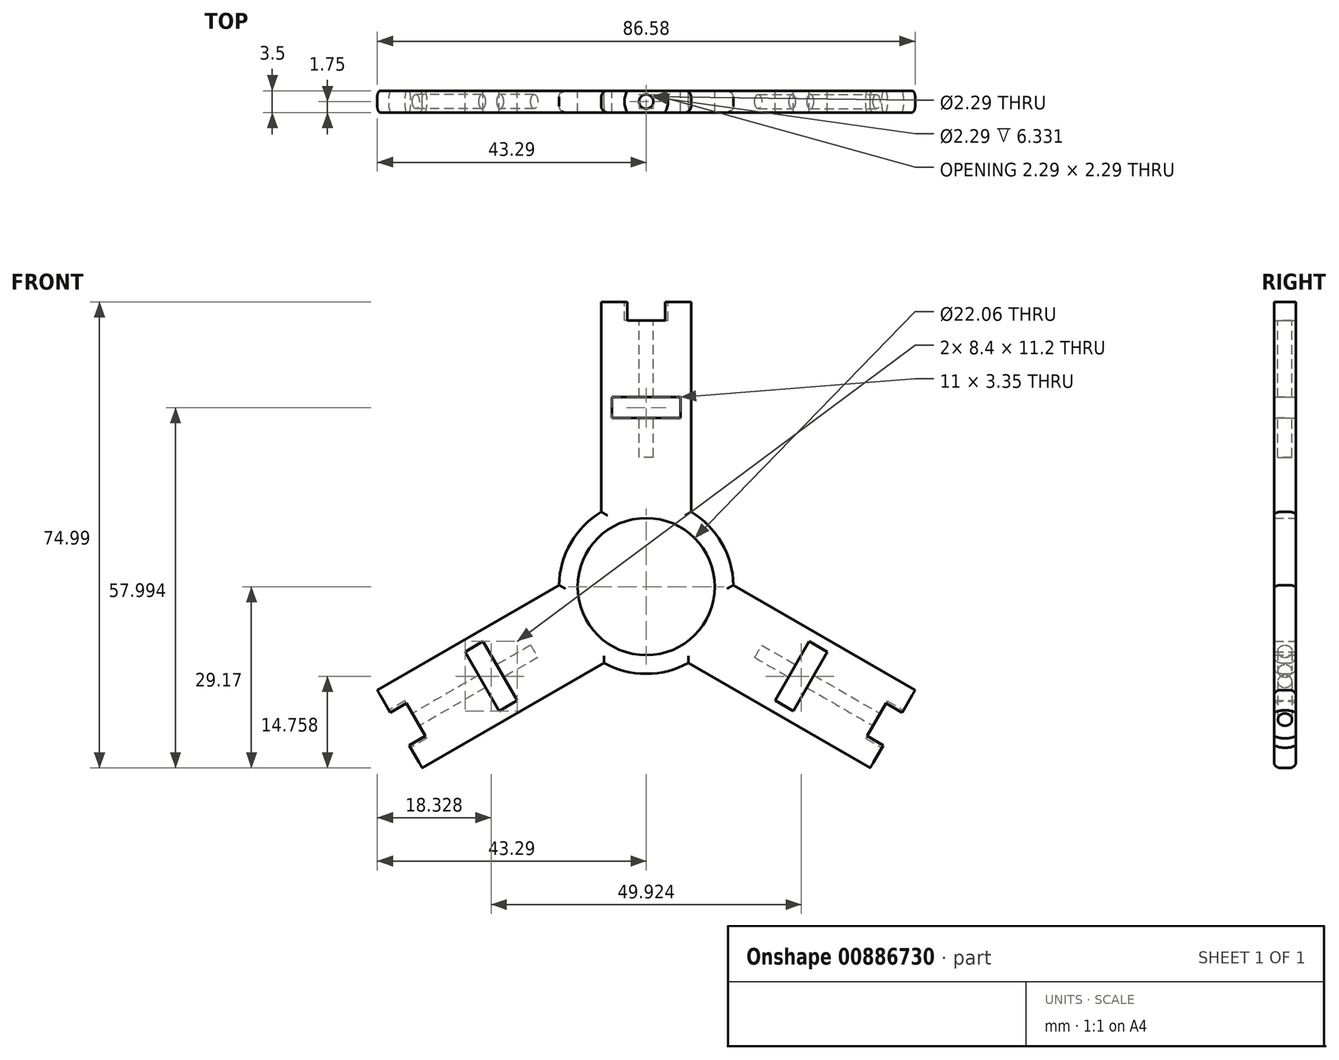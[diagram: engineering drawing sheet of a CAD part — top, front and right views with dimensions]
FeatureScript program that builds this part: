
annotation { "Feature Type Name" : "Feature", "Feature Type Description" : "" }
export const myFeature = defineFeature(function(context is Context, id is Id, definition is map)
    precondition{}
    {
        {
            var Q0;
            Q0=qCreatedBy(makeId("Front.planeOp"),FACE);
            var sketch = newSketch(context, id + "F0", { "sketchPlane" : qUnion([Q0])});
            skCircle(sketch, "E0", {"center": v(0, 0) * mm, "radius": 11.03 * mm});
            skCircle(sketch, "E1.0", {"center": v(0, 0) * mm, "radius": 14.03 * mm});
            skSolve(sketch);
        }
        {
            var Q0;
            Q0=qCreatedBy(makeId("Front.planeOp"),FACE);
            var sketch = newSketch(context, id + "F1", { "sketchPlane" : qUnion([Q0])});
            skLineSegment(sketch, "E2.bottom", {"start": v(0, 0) * mm, "end": v(-7.23, 0) * mm});
            skLineSegment(sketch, "E2.top", {"start": v(0, 45.82) * mm, "end": v(-7.23, 45.82) * mm});
            skLineSegment(sketch, "E2.left", {"start": v(0, 0) * mm, "end": v(0, 45.82) * mm});
            skLineSegment(sketch, "E2.right", {"start": v(-7.23, 0) * mm, "end": v(-7.23, 45.82) * mm});
            skLineSegment(sketch, "E3.MirrorCS", {"start": v(0, 0) * mm, "end": v(7.23, 0) * mm});
            skLineSegment(sketch, "E4.MirrorCS", {"start": v(0, 45.82) * mm, "end": v(7.23, 45.82) * mm});
            skLineSegment(sketch, "E5.MirrorCS", {"start": v(7.23, 0) * mm, "end": v(7.23, 45.82) * mm});
            skSolve(sketch);
        }
        {
            var Q0;
            Q0=makeQuery(id+"F0.imprint","IMPRINT",FACE,{"disambiguationData":[TD([[makeQuery(id+"F0.imprint","IMPRINT",EDGE,{"derivedFrom":sQuery(id+"F0.wireOp",EDGE,"E0")}),-1.0]])]});
            extrude(context, id + "F2", {"entities" : qUnion([Q0]), "endBound" : BoundingType.SYMMETRIC, "depth" : 3.5 * mm, "offsetDistance" : 25 * mm});
        }
        {
            var Q0;
            Q0=makeQuery(id+"F1.imprint","IMPRINT",FACE,{"disambiguationData":[TD([[makeQuery(id+"F1.imprint","IMPRINT",EDGE,{"derivedFrom":sQuery(id+"F1.wireOp",EDGE,"E2.left")}),-1.0]])]});
            var Q1;
            Q1=makeQuery(id+"F1.imprint","IMPRINT",FACE,{"disambiguationData":[TD([[makeQuery(id+"F1.imprint","IMPRINT",EDGE,{"derivedFrom":sQuery(id+"F1.wireOp",EDGE,"E2.bottom")}),-1.0]])]});
            extrude(context, id + "F3", {"entities" : qUnion([Q0, Q1]), "operationType" : NewBodyOperationType.ADD, "endBound" : BoundingType.SYMMETRIC, "depth" : 3.5 * mm, "offsetDistance" : 25 * mm});
        }
        {
            var Q0;
            Q0=makeQuery(id+"F3.opExtrude","SWEPT_FACE",FACE,{"disambiguationData":[OSD([sQuery(id+"F1.wireOp",EDGE,"E2.top"),sQuery(id+"F1.wireOp",EDGE,"E4.MirrorCS")])]});
            var sketch = newSketch(context, id + "F4", { "sketchPlane" : qUnion([Q0])});
            skCircle(sketch, "E6", {"center": v(0, 0) * mm, "radius": 3.5 * mm});
            skCircle(sketch, "E7", {"center": v(0, 0) * mm, "radius": 1.14 * mm});
            skSolve(sketch);
        }
        {
            var Q0;
            {var subQ0=sQuery(id+"F4.wireOp",EDGE,"E6");var subQ1=makeQuery(id+"F3.opExtrude","CAP_EDGE",EDGE,{"disambiguationData":[OSD([sQuery(id+"F1.wireOp",EDGE,"E2.top"),sQuery(id+"F1.wireOp",EDGE,"E4.MirrorCS")])],"isStart":false});var subQ2=makeQuery(id+"F4.imprint","INTERSECT",VERTEX,{"disambiguationData":[OD(0.0)],"derivedFrom":[subQ1,subQ0]});Q0=makeQuery(id+"F4.imprint","IMPRINT",FACE,{"disambiguationData":[TD([[makeQuery(id+"F4.imprint","IMPRINT",EDGE,{"disambiguationData":[TD([[subQ2,-1.0]])],"derivedFrom":subQ0}),1.0]])]});}
            var Q1;
            Q1=makeQuery(id+"F4.imprint","IMPRINT",FACE,{"disambiguationData":[TD([[makeQuery(id+"F4.imprint","IMPRINT",EDGE,{"derivedFrom":sQuery(id+"F4.wireOp",EDGE,"E7")}),-1.0]])]});
            var Q2;
            {var subQ0=sQuery(id+"F4.wireOp",EDGE,"E6");var subQ1=makeQuery(id+"F3.opExtrude","CAP_EDGE",EDGE,{"disambiguationData":[OSD([sQuery(id+"F1.wireOp",EDGE,"E2.top"),sQuery(id+"F1.wireOp",EDGE,"E4.MirrorCS")])],"isStart":true});var subQ2=makeQuery(id+"F4.imprint","INTERSECT",VERTEX,{"disambiguationData":[OD(0.0)],"derivedFrom":[subQ1,subQ0]});Q2=makeQuery(id+"F4.imprint","IMPRINT",FACE,{"disambiguationData":[TD([[makeQuery(id+"F4.imprint","IMPRINT",EDGE,{"disambiguationData":[TD([[subQ2,1.0]])],"derivedFrom":subQ0}),1.0]])]});}
            var Q3;
            Q3=makeQuery(id+"F4.imprint","IMPRINT",FACE,{"disambiguationData":[TD([[makeQuery(id+"F4.imprint","IMPRINT",EDGE,{"derivedFrom":sQuery(id+"F4.wireOp",EDGE,"E7")}),1.0]])]});
            extrude(context, id + "F5", {"entities" : qUnion([Q0, Q1, Q2, Q3]), "operationType" : NewBodyOperationType.REMOVE, "oppositeDirection" : true, "depth" : 3 * mm, "offsetDistance" : 25 * mm});
        }
        {
            var Q0;
            Q0=makeQuery(id+"F4.imprint","IMPRINT",FACE,{"disambiguationData":[TD([[makeQuery(id+"F4.imprint","IMPRINT",EDGE,{"derivedFrom":sQuery(id+"F4.wireOp",EDGE,"E7")}),1.0]])]});
            extrude(context, id + "F6", {"entities" : qUnion([Q0]), "operationType" : NewBodyOperationType.REMOVE, "oppositeDirection" : true, "depth" : 25 * mm, "offsetDistance" : 25 * mm});
        }
        {
            var Q0;
            Q0=makeQuery(id+"F3.boolean.opBoolean","MERGE",FACE,{"derivedFrom":[makeQuery(id+"F2.opExtrude","CAP_FACE",FACE,{"disambiguationData":[OSD([sQuery(id+"F0.wireOp",EDGE,"E0")])],"isStart":true}),makeQuery(id+"F3.opExtrude","CAP_FACE",FACE,{"disambiguationData":[OSD([sQuery(id+"F1.wireOp",EDGE,"E2.bottom"),sQuery(id+"F1.wireOp",EDGE,"E2.top"),sQuery(id+"F1.wireOp",EDGE,"E2.right"),sQuery(id+"F1.wireOp",EDGE,"E3.MirrorCS"),sQuery(id+"F1.wireOp",EDGE,"E4.MirrorCS"),sQuery(id+"F1.wireOp",EDGE,"E5.MirrorCS")])],"isStart":true})]});
            var sketch = newSketch(context, id + "F7", { "sketchPlane" : qUnion([Q0])});
            skLineSegment(sketch, "E8.bottom", {"start": v(0, 27.15) * mm, "end": v(5.5, 27.15) * mm});
            skLineSegment(sketch, "E8.top", {"start": v(0, 30.5) * mm, "end": v(5.5, 30.5) * mm});
            skLineSegment(sketch, "E8.left", {"start": v(0, 27.15) * mm, "end": v(0, 30.5) * mm});
            skLineSegment(sketch, "E8.right", {"start": v(5.5, 27.15) * mm, "end": v(5.5, 30.5) * mm});
            skLineSegment(sketch, "E9.MirrorCS", {"start": v(0, 30.5) * mm, "end": v(-5.5, 30.5) * mm});
            skLineSegment(sketch, "E10.MirrorCS", {"start": v(-5.5, 27.15) * mm, "end": v(-5.5, 30.5) * mm});
            skLineSegment(sketch, "E11.MirrorCS", {"start": v(0, 27.15) * mm, "end": v(-5.5, 27.15) * mm});
            skSolve(sketch);
        }
        {
            var Q0;
            Q0=qCreatedBy(makeId("Top.planeOp"),FACE);
            var sketch = newSketch(context, id + "F8", { "sketchPlane" : qUnion([Q0])});
            skLineSegment(sketch, "E12", {"start": v(0, 0) * mm, "end": v(0, 39.45) * mm});
            skLineSegment(sketch, "E13", {"start": v(0, 39.45) * mm, "end": v(0, 0) * mm, "construction": true});
            skSolve(sketch);
        }
        {
            var Q0;
            Q0=qSketchRegion(id+"F7",true);
            extrude(context, id + "F9", {"entities" : qUnion([Q0]), "operationType" : NewBodyOperationType.REMOVE, "endBound" : BoundingType.SYMMETRIC, "oppositeDirection" : true, "depth" : 25 * mm, "offsetDistance" : 25 * mm});
        }
        {
            var Q0;
            Q0=makeQuery(id+"F2.opExtrude","SWEPT_BODY",BODY,{"disambiguationData":[OSD([sQuery(id+"F0.wireOp",EDGE,"E0"),sQuery(id+"F0.wireOp",EDGE,"E1.0")])]});
            var Q1;
            Q1=sQuery(id+"F8.wireOp",EDGE,"E12");
            circularPattern(context, id + "F10", {"entities" : qUnion([Q0]), "axis" : qUnion([Q1]), "angle" : 360 * degree, "instanceCount" : 3, "equalSpace" : true});
        }
        {
            var Q0;
            Q0=makeQuery(id+"F0.imprint","IMPRINT",FACE,{"disambiguationData":[TD([[makeQuery(id+"F0.imprint","IMPRINT",EDGE,{"derivedFrom":sQuery(id+"F0.wireOp",EDGE,"E0")}),1.0]])]});
            extrude(context, id + "F11", {"entities" : qUnion([Q0]), "operationType" : NewBodyOperationType.REMOVE, "endBound" : BoundingType.SYMMETRIC, "depth" : 25 * mm, "offsetDistance" : 25 * mm});
        }
        {
            var Q0;
            Q0=makeQuery(id+"F10.opPattern","COPY",EDGE,{"derivedFrom":makeQuery(id+"F2.opExtrude","CAP_EDGE",EDGE,{"disambiguationData":[OSD([sQuery(id+"F0.wireOp",EDGE,"E1.0")])],"isStart":true}),"instanceName":"1"});
            var Q1;
            Q1=makeQuery(id+"F10.opPattern","COPY",EDGE,{"derivedFrom":makeQuery(id+"F2.opExtrude","CAP_EDGE",EDGE,{"disambiguationData":[OSD([sQuery(id+"F0.wireOp",EDGE,"E1.0")])],"isStart":true}),"instanceName":"2"});
            var Q2;
            Q2=makeQuery(id+"F10.opPattern","COPY",EDGE,{"derivedFrom":makeQuery(id+"F2.opExtrude","CAP_EDGE",EDGE,{"disambiguationData":[OSD([sQuery(id+"F0.wireOp",EDGE,"E1.0")])],"isStart":false}),"instanceName":"2"});
            fillet(context, id + "F12", {"entities" : qUnion([Q0, Q1, Q2]), "radius" : 2 * mm, "tangentPropagation" : true, "allowEdgeOverflow" : false});
        }
        {
            var Q0;
            Q0=makeQuery(id+"F2.opExtrude","SWEPT_BODY",BODY,{"disambiguationData":[OSD([sQuery(id+"F0.wireOp",EDGE,"E0"),sQuery(id+"F0.wireOp",EDGE,"E1.0")])]});
            var Q1;
            Q1=makeQuery(id+"F10.opPattern","COPY",BODY,{"derivedFrom":makeQuery(id+"F2.opExtrude","SWEPT_BODY",BODY,{"disambiguationData":[OSD([sQuery(id+"F0.wireOp",EDGE,"E0"),sQuery(id+"F0.wireOp",EDGE,"E1.0")])]}),"instanceName":"1"});
            var Q2;
            Q2=makeQuery(id+"F10.opPattern","COPY",BODY,{"derivedFrom":makeQuery(id+"F2.opExtrude","SWEPT_BODY",BODY,{"disambiguationData":[OSD([sQuery(id+"F0.wireOp",EDGE,"E0"),sQuery(id+"F0.wireOp",EDGE,"E1.0")])]}),"instanceName":"2"});
            booleanBodies(context, id + "F13", {"operationType" : BooleanOperationType.UNION, "tools" : qUnion([Q0, Q1, Q2])});
        }
        {
            var Q0;
            {var subQ0=sQuery(id+"F0.wireOp",EDGE,"E1.0");var subQ1=makeQuery(id+"F2.opExtrude","SWEPT_FACE",FACE,{"disambiguationData":[OSD([subQ0])]});var subQ4=sQuery(id+"F1.wireOp",EDGE,"E5.MirrorCS");Q0=makeQuery(id+"F13.opBoolean","SPLIT",EDGE,{"disambiguationData":[TD([makeQuery(id+"F10.opPattern","COPY",FACE,{"derivedFrom":makeQuery(id+"F3.boolean.opBoolean","SPLIT",FACE,{"disambiguationData":[TD([subQ1])],"derivedFrom":makeQuery(id+"F3.opExtrude","SWEPT_FACE",FACE,{"disambiguationData":[OSD([subQ4])]})}),"instanceName":"1"})])],"derivedFrom":makeQuery(id+"F2.opExtrude","CAP_EDGE",EDGE,{"disambiguationData":[OSD([subQ0])],"isStart":true})});}
            var Q1;
            {var subQ2=sQuery(id+"F0.wireOp",EDGE,"E1.0");var subQ3=sQuery(id+"F1.wireOp",EDGE,"E5.MirrorCS");Q1=makeQuery(id+"F10.opPattern","COPY",EDGE,{"derivedFrom":makeQuery(id+"F3.boolean.opBoolean","SPLIT",EDGE,{"disambiguationData":[TD([makeQuery(id+"F2.opExtrude","SWEPT_FACE",FACE,{"disambiguationData":[OSD([subQ2])]})])],"derivedFrom":makeQuery(id+"F3.opExtrude","CAP_EDGE",EDGE,{"disambiguationData":[OSD([subQ3])],"isStart":true})}),"instanceName":"1"});}
            var Q2;
            {var subQ2=sQuery(id+"F0.wireOp",EDGE,"E1.0");var subQ3=sQuery(id+"F1.wireOp",EDGE,"E2.right");Q2=makeQuery(id+"F10.opPattern","COPY",EDGE,{"derivedFrom":makeQuery(id+"F3.boolean.opBoolean","SPLIT",EDGE,{"disambiguationData":[TD([makeQuery(id+"F2.opExtrude","SWEPT_FACE",FACE,{"disambiguationData":[OSD([subQ2])]})])],"derivedFrom":makeQuery(id+"F3.opExtrude","CAP_EDGE",EDGE,{"disambiguationData":[OSD([subQ3])],"isStart":true})}),"instanceName":"2"});}
            var Q3;
            {var subQ2=sQuery(id+"F0.wireOp",EDGE,"E1.0");var subQ3=sQuery(id+"F1.wireOp",EDGE,"E5.MirrorCS");Q3=makeQuery(id+"F10.opPattern","COPY",EDGE,{"derivedFrom":makeQuery(id+"F3.boolean.opBoolean","SPLIT",EDGE,{"disambiguationData":[TD([makeQuery(id+"F2.opExtrude","SWEPT_FACE",FACE,{"disambiguationData":[OSD([subQ2])]})])],"derivedFrom":makeQuery(id+"F3.opExtrude","CAP_EDGE",EDGE,{"disambiguationData":[OSD([subQ3])],"isStart":true})}),"instanceName":"2"});}
            var Q4;
            {var subQ0=sQuery(id+"F1.wireOp",EDGE,"E2.right");var subQ1=sQuery(id+"F0.wireOp",EDGE,"E1.0");Q4=makeQuery(id+"F13.opBoolean","SPLIT",EDGE,{"disambiguationData":[TD([makeQuery(id+"F3.opExtrude","SWEPT_FACE",FACE,{"disambiguationData":[OSD([subQ0])]})])],"derivedFrom":makeQuery(id+"F2.opExtrude","CAP_EDGE",EDGE,{"disambiguationData":[OSD([subQ1])],"isStart":true})});}
            var Q5;
            {var subQ2=sQuery(id+"F0.wireOp",EDGE,"E1.0");var subQ3=sQuery(id+"F1.wireOp",EDGE,"E2.right");Q5=makeQuery(id+"F3.boolean.opBoolean","SPLIT",EDGE,{"disambiguationData":[TD([makeQuery(id+"F2.opExtrude","SWEPT_FACE",FACE,{"disambiguationData":[OSD([subQ2])]})])],"derivedFrom":makeQuery(id+"F3.opExtrude","CAP_EDGE",EDGE,{"disambiguationData":[OSD([subQ3])],"isStart":true})});}
            var Q6;
            {var subQ2=sQuery(id+"F0.wireOp",EDGE,"E1.0");var subQ3=sQuery(id+"F1.wireOp",EDGE,"E5.MirrorCS");Q6=makeQuery(id+"F3.boolean.opBoolean","SPLIT",EDGE,{"disambiguationData":[TD([makeQuery(id+"F2.opExtrude","SWEPT_FACE",FACE,{"disambiguationData":[OSD([subQ2])]})])],"derivedFrom":makeQuery(id+"F3.opExtrude","CAP_EDGE",EDGE,{"disambiguationData":[OSD([subQ3])],"isStart":true})});}
            var Q7;
            {var subQ0=sQuery(id+"F0.wireOp",EDGE,"E1.0");var subQ2=sQuery(id+"F1.wireOp",EDGE,"E5.MirrorCS");Q7=makeQuery(id+"F13.opBoolean","SPLIT",EDGE,{"disambiguationData":[TD([makeQuery(id+"F3.opExtrude","SWEPT_FACE",FACE,{"disambiguationData":[OSD([subQ2])]})])],"derivedFrom":makeQuery(id+"F2.opExtrude","CAP_EDGE",EDGE,{"disambiguationData":[OSD([subQ0])],"isStart":true})});}
            var Q8;
            {var subQ2=sQuery(id+"F0.wireOp",EDGE,"E1.0");var subQ3=sQuery(id+"F1.wireOp",EDGE,"E2.right");Q8=makeQuery(id+"F10.opPattern","COPY",EDGE,{"derivedFrom":makeQuery(id+"F3.boolean.opBoolean","SPLIT",EDGE,{"disambiguationData":[TD([makeQuery(id+"F2.opExtrude","SWEPT_FACE",FACE,{"disambiguationData":[OSD([subQ2])]})])],"derivedFrom":makeQuery(id+"F3.opExtrude","CAP_EDGE",EDGE,{"disambiguationData":[OSD([subQ3])],"isStart":true})}),"instanceName":"1"});}
            var Q9;
            {var subQ2=sQuery(id+"F0.wireOp",EDGE,"E1.0");var subQ3=sQuery(id+"F1.wireOp",EDGE,"E5.MirrorCS");Q9=makeQuery(id+"F10.opPattern","COPY",EDGE,{"derivedFrom":makeQuery(id+"F3.boolean.opBoolean","SPLIT",EDGE,{"disambiguationData":[TD([makeQuery(id+"F2.opExtrude","SWEPT_FACE",FACE,{"disambiguationData":[OSD([subQ2])]})])],"derivedFrom":makeQuery(id+"F3.opExtrude","CAP_EDGE",EDGE,{"disambiguationData":[OSD([subQ3])],"isStart":false})}),"instanceName":"1"});}
            var Q10;
            {var subQ2=sQuery(id+"F0.wireOp",EDGE,"E1.0");var subQ3=sQuery(id+"F1.wireOp",EDGE,"E2.right");Q10=makeQuery(id+"F10.opPattern","COPY",EDGE,{"derivedFrom":makeQuery(id+"F3.boolean.opBoolean","SPLIT",EDGE,{"disambiguationData":[TD([makeQuery(id+"F2.opExtrude","SWEPT_FACE",FACE,{"disambiguationData":[OSD([subQ2])]})])],"derivedFrom":makeQuery(id+"F3.opExtrude","CAP_EDGE",EDGE,{"disambiguationData":[OSD([subQ3])],"isStart":false})}),"instanceName":"2"});}
            var Q11;
            {var subQ0=sQuery(id+"F0.wireOp",EDGE,"E1.0");var subQ1=makeQuery(id+"F2.opExtrude","SWEPT_FACE",FACE,{"disambiguationData":[OSD([subQ0])]});var subQ4=sQuery(id+"F1.wireOp",EDGE,"E5.MirrorCS");Q11=makeQuery(id+"F13.opBoolean","SPLIT",EDGE,{"disambiguationData":[TD([makeQuery(id+"F10.opPattern","COPY",FACE,{"derivedFrom":makeQuery(id+"F3.boolean.opBoolean","SPLIT",FACE,{"disambiguationData":[TD([subQ1])],"derivedFrom":makeQuery(id+"F3.opExtrude","SWEPT_FACE",FACE,{"disambiguationData":[OSD([subQ4])]})}),"instanceName":"1"})])],"derivedFrom":makeQuery(id+"F2.opExtrude","CAP_EDGE",EDGE,{"disambiguationData":[OSD([subQ0])],"isStart":false})});}
            var Q12;
            {var subQ0=sQuery(id+"F1.wireOp",EDGE,"E5.MirrorCS");var subQ1=sQuery(id+"F0.wireOp",EDGE,"E1.0");Q12=makeQuery(id+"F13.opBoolean","SPLIT",EDGE,{"disambiguationData":[TD([makeQuery(id+"F3.opExtrude","SWEPT_FACE",FACE,{"disambiguationData":[OSD([subQ0])]})])],"derivedFrom":makeQuery(id+"F2.opExtrude","CAP_EDGE",EDGE,{"disambiguationData":[OSD([subQ1])],"isStart":false})});}
            var Q13;
            {var subQ0=sQuery(id+"F1.wireOp",EDGE,"E2.right");var subQ7=sQuery(id+"F0.wireOp",EDGE,"E1.0");Q13=makeQuery(id+"F13.opBoolean","SPLIT",EDGE,{"disambiguationData":[TD([makeQuery(id+"F3.opExtrude","SWEPT_FACE",FACE,{"disambiguationData":[OSD([subQ0])]})])],"derivedFrom":makeQuery(id+"F2.opExtrude","CAP_EDGE",EDGE,{"disambiguationData":[OSD([subQ7])],"isStart":false})});}
            var Q14;
            {var subQ2=sQuery(id+"F0.wireOp",EDGE,"E1.0");var subQ3=sQuery(id+"F1.wireOp",EDGE,"E5.MirrorCS");Q14=makeQuery(id+"F10.opPattern","COPY",EDGE,{"derivedFrom":makeQuery(id+"F3.boolean.opBoolean","SPLIT",EDGE,{"disambiguationData":[TD([makeQuery(id+"F2.opExtrude","SWEPT_FACE",FACE,{"disambiguationData":[OSD([subQ2])]})])],"derivedFrom":makeQuery(id+"F3.opExtrude","CAP_EDGE",EDGE,{"disambiguationData":[OSD([subQ3])],"isStart":false})}),"instanceName":"2"});}
            var Q15;
            {var subQ2=sQuery(id+"F0.wireOp",EDGE,"E1.0");var subQ3=sQuery(id+"F1.wireOp",EDGE,"E5.MirrorCS");Q15=makeQuery(id+"F3.boolean.opBoolean","SPLIT",EDGE,{"disambiguationData":[TD([makeQuery(id+"F2.opExtrude","SWEPT_FACE",FACE,{"disambiguationData":[OSD([subQ2])]})])],"derivedFrom":makeQuery(id+"F3.opExtrude","CAP_EDGE",EDGE,{"disambiguationData":[OSD([subQ3])],"isStart":false})});}
            var Q16;
            {var subQ2=sQuery(id+"F0.wireOp",EDGE,"E1.0");var subQ3=sQuery(id+"F1.wireOp",EDGE,"E2.right");Q16=makeQuery(id+"F10.opPattern","COPY",EDGE,{"derivedFrom":makeQuery(id+"F3.boolean.opBoolean","SPLIT",EDGE,{"disambiguationData":[TD([makeQuery(id+"F2.opExtrude","SWEPT_FACE",FACE,{"disambiguationData":[OSD([subQ2])]})])],"derivedFrom":makeQuery(id+"F3.opExtrude","CAP_EDGE",EDGE,{"disambiguationData":[OSD([subQ3])],"isStart":false})}),"instanceName":"1"});}
            var Q17;
            {var subQ2=sQuery(id+"F0.wireOp",EDGE,"E1.0");var subQ3=sQuery(id+"F1.wireOp",EDGE,"E2.right");Q17=makeQuery(id+"F3.boolean.opBoolean","SPLIT",EDGE,{"disambiguationData":[TD([makeQuery(id+"F2.opExtrude","SWEPT_FACE",FACE,{"disambiguationData":[OSD([subQ2])]})])],"derivedFrom":makeQuery(id+"F3.opExtrude","CAP_EDGE",EDGE,{"disambiguationData":[OSD([subQ3])],"isStart":false})});}
            fillet(context, id + "F14", {"entities" : qUnion([Q0, Q1, Q2, Q3, Q4, Q5, Q6, Q7, Q8, Q9, Q10, Q11, Q12, Q13, Q14, Q15, Q16, Q17]), "radius" : 1 * mm, "tangentPropagation" : true, "allowEdgeOverflow" : false});
        }
    });
